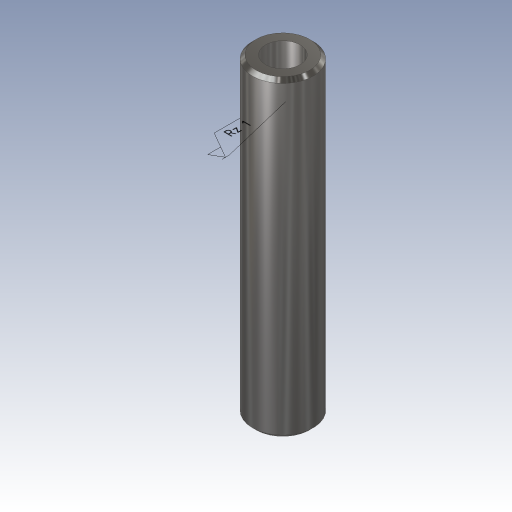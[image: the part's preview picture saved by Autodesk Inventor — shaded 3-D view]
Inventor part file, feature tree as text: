
AUTODESK INVENTOR PART (.ipt)
format: ipt  version: 2023.3 (Build 273359000, 359)  size: 144,896 bytes
history: native  units: in
note: dims shown in document units (in); Inventor stores cm internally (conversion verified against a paired STEP export)
features: other x2, extrude x1, chamfer x1, sketch x1
ambient origin geometry x8: Origin, YZ Plane, XZ Plane, XY Plane, X Axis, Y Axis, Z Axis, Center Point
bodies: Body1 (feature_tree)
feature tree (5):
  other  "Anmerkungen"
  extrude  "Extrusion3"  Depth=0.7087in
  chamfer  "Fase1"  Distance=0.7087in
  sketch  "Skizze3"  dims[d4=0.0787in d5=0.0295in d6=0.7087in d7=0.0in d8=0.0079in d9=0.0787in d10=45.0deg d11=0.3689in d12=0.1044in]
  other  "Oberflächenbeschaffenheit 1"
